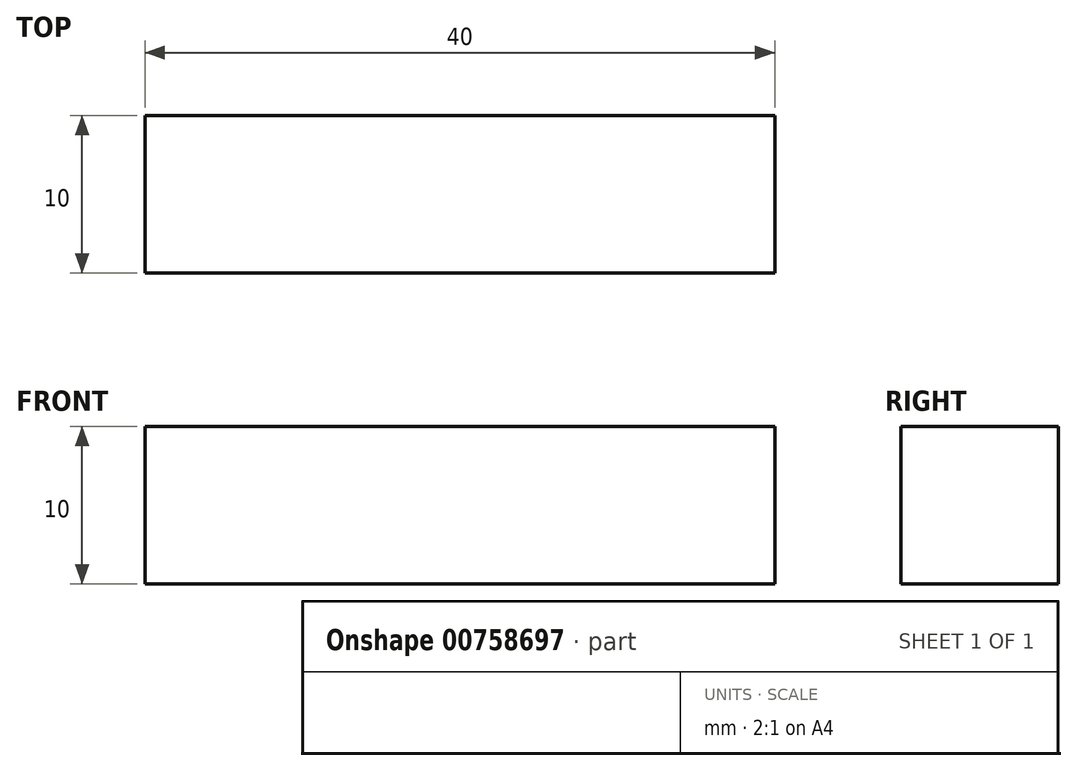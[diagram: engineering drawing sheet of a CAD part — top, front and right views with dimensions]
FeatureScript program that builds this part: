
annotation { "Feature Type Name" : "Feature", "Feature Type Description" : "" }
export const myFeature = defineFeature(function(context is Context, id is Id, definition is map)
    precondition{}
    {
        {
            var Q0;
            Q0=qCreatedBy(makeId("Front.planeOp"),FACE);
            var sketch = newSketch(context, id + "F0", { "sketchPlane" : qUnion([Q0])});
            skLineSegment(sketch, "E0.bottom", {"start": v(-20, 5) * mm, "end": v(20, 5) * mm});
            skLineSegment(sketch, "E0.top", {"start": v(-20, -5) * mm, "end": v(20, -5) * mm});
            skLineSegment(sketch, "E0.left", {"start": v(-20, 5) * mm, "end": v(-20, -5) * mm});
            skLineSegment(sketch, "E0.right", {"start": v(20, 5) * mm, "end": v(20, -5) * mm});
            skPoint(sketch, "E0.middle", {"position": v(0, 0) * mm});
            skSolve(sketch);
        }
        {
            var Q0;
            Q0 = qSketchRegion(id + "F0", true);
            extrude(context, id + "F1", {"entities" : qUnion([Q0]), "endBound" : BoundingType.SYMMETRIC, "depth" : 10 * mm, "offsetDistance" : 25.4 * mm});
        }
    });
